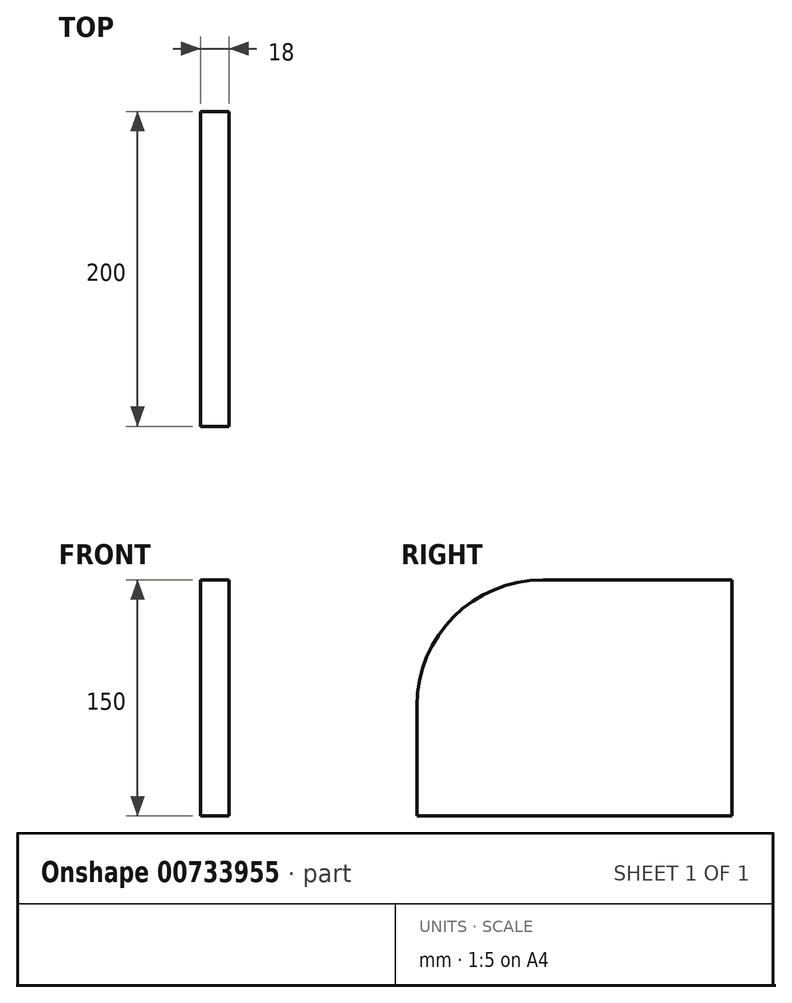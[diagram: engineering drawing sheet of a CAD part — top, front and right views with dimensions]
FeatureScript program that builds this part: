
annotation { "Feature Type Name" : "Feature", "Feature Type Description" : "" }
export const myFeature = defineFeature(function(context is Context, id is Id, definition is map)
    precondition{}
    {
        {
            var Q0;
            Q0=qCreatedBy(makeId("Right.planeOp"),FACE);
            var sketch = newSketch(context, id + "F0", { "sketchPlane" : qUnion([Q0])});
            skLineSegment(sketch, "E0.bottom", {"start": v(0, 0) * mm, "end": v(200, 0) * mm});
            skLineSegment(sketch, "E0.top", {"start": v(80, 150) * mm, "end": v(200, 150) * mm});
            skLineSegment(sketch, "E0.left", {"start": v(0, 0) * mm, "end": v(0, 70) * mm});
            skLineSegment(sketch, "E0.right", {"start": v(200, 0) * mm, "end": v(200, 150) * mm});
            skPoint(sketch, "E1.visualSharp", {"position": v(0, 150) * mm});
            skArc(sketch, "E1.filletArc", {"start": v(80, 150) * mm, "mid": v(23.43, 126.57) * mm, "end": v(0, 70) * mm});
            skSolve(sketch);
        }
        {
            var Q0;
            Q0 = qSketchRegion(id + "F0", true);
            extrude(context, id + "F1", {"entities" : qUnion([Q0]), "oppositeDirection" : true, "depth" : 18 * mm, "offsetDistance" : 25 * mm});
        }
    });
